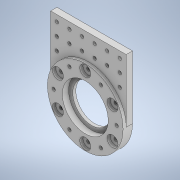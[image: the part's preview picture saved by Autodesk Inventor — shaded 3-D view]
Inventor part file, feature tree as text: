
AUTODESK INVENTOR PART (.ipt)
format: ipt  version: 2020 (Build 240168000, 168)  size: 261,632 bytes
history: native  units: in
note: dims shown in document units (in); Inventor stores cm internally (conversion verified against a paired STEP export)
features: extrude x6, sketch x6, projected_geometry x1
ambient origin geometry x8: Origin, YZ Plane, XZ Plane, XY Plane, X Axis, Y Axis, Z Axis, Center Point
bodies: Solid1 (feature_tree)
feature tree (13):
  extrude  "Extrusion1"  Depth=6.0in
  extrude  "Extrusion2"  Depth=3.0in
  extrude  "Extrusion3"  Depth=0.25in TaperAngle=0.0deg
  extrude  "Extrusion4"  Depth=0.25in
  extrude  "Extrusion5"  Depth=0.5in TaperAngle=0.0deg
  extrude  "Extrusion6"  Depth=0.5in TaperAngle=360.0deg
  sketch  "Sketch1"  dims[d0=2.5in d1=6.0in]
  sketch  "Sketch2"  dims[d2=0.2656in d3=3.0in]
  sketch  "Sketch3"  dims[d4=4.7244in d6=360.0deg d8=0.25in d9=0.0in]
  projected_geometry  "Projected Loop1"
  sketch  "Sketch4"  dims[d10=3.6407in d11=0.25in]
  sketch  "Sketch5"  dims[d12=0.5in d13=0.0in d14=0.5in d15=0.0in]
  sketch  "Sketch6"  dims[d16=0.875in d17=2.3622in d19=360.0deg d21=0.25in d22=0.0in d23=5.0in d24=0.5in d25=0.0in d26=0.2656in d27=2.5in d28=4.5in d29=1.1811in d31=1.0in d32=2.3622in d34=1.0in d37=0.0in d38=0.0in d39=0.5in d40=0.0344in d41=0.5in d42=0.0344in d45=0.5in d46=0.0344in d47=0.5in d48=0.0344in]
